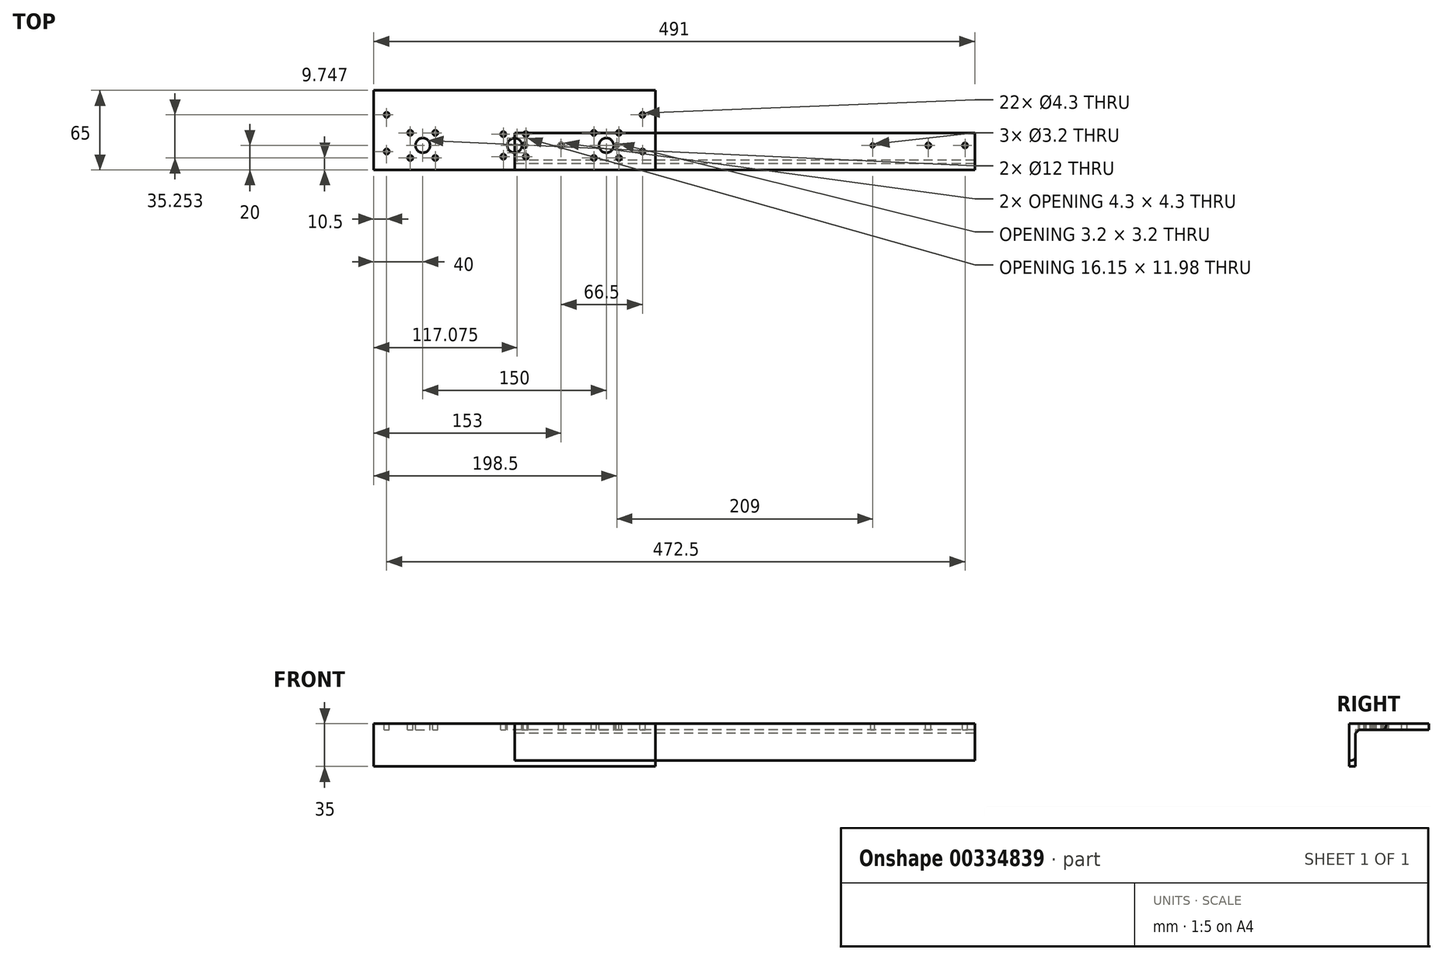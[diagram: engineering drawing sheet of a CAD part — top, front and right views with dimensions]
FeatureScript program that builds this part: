
annotation { "Feature Type Name" : "Feature", "Feature Type Description" : "" }
export const myFeature = defineFeature(function(context is Context, id is Id, definition is map)
    precondition{}
    {
        {
            var Q0;
            Q0=qCreatedBy(makeId("Right.planeOp"),FACE);
            var sketch = newSketch(context, id + "F0", { "sketchPlane" : qUnion([Q0])});
            skLineSegment(sketch, "E0", {"start": v(0, -35) * mm, "end": v(0, 0) * mm});
            skLineSegment(sketch, "E1", {"start": v(0, 0) * mm, "end": v(65, 0) * mm});
            skLineSegment(sketch, "E2", {"start": v(65, 0) * mm, "end": v(65, -5) * mm});
            skLineSegment(sketch, "E3", {"start": v(65, -5) * mm, "end": v(5, -5) * mm});
            skLineSegment(sketch, "E4", {"start": v(5, -5) * mm, "end": v(5, -35) * mm});
            skLineSegment(sketch, "E5", {"start": v(5, -35) * mm, "end": v(0, -35) * mm});
            skSolve(sketch);
        }
        {
            var Q0;
            Q0=qCreatedBy(makeId("Right.planeOp"),FACE);
            var sketch = newSketch(context, id + "F1", { "sketchPlane" : qUnion([Q0])});
            skLineSegment(sketch, "E6", {"start": v(0, -30) * mm, "end": v(0, 0) * mm});
            skLineSegment(sketch, "E7", {"start": v(0, 0) * mm, "end": v(30, 0) * mm});
            skLineSegment(sketch, "E8", {"start": v(30, 0) * mm, "end": v(30, -2) * mm});
            skLineSegment(sketch, "E9", {"start": v(27, -5) * mm, "end": v(5, -5) * mm});
            skLineSegment(sketch, "E10", {"start": v(5, -5) * mm, "end": v(5, -27) * mm});
            skLineSegment(sketch, "E11", {"start": v(2, -30) * mm, "end": v(0, -30) * mm});
            skPoint(sketch, "E12.visualSharp", {"position": v(30, -5) * mm});
            skArc(sketch, "E12.filletArc", {"start": v(27, -5) * mm, "mid": v(29.12, -4.12) * mm, "end": v(30, -2) * mm});
            skPoint(sketch, "E13.visualSharp", {"position": v(5, -30) * mm});
            skArc(sketch, "E13.filletArc", {"start": v(2, -30) * mm, "mid": v(4.12, -29.12) * mm, "end": v(5, -27) * mm});
            skLineSegment(sketch, "E14", {"start": v(5, -8) * mm, "end": v(8, -5) * mm});
            skSolve(sketch);
        }
        {
            var Q0;
            Q0=qCreatedBy(makeId("Right.planeOp"),FACE);
            var sketch = newSketch(context, id + "F2", { "sketchPlane" : qUnion([Q0])});
            skLineSegment(sketch, "E15", {"start": v(0, 0) * mm, "end": v(20, 0) * mm});
            skLineSegment(sketch, "E16", {"start": v(20, 0) * mm, "end": v(20, 0) * mm});
            skLineSegment(sketch, "E17", {"start": v(17, -3) * mm, "end": v(6, -3) * mm});
            skLineSegment(sketch, "E18", {"start": v(3, -6) * mm, "end": v(3, -17) * mm});
            skLineSegment(sketch, "E19", {"start": v(0, -20) * mm, "end": v(0, -20) * mm});
            skLineSegment(sketch, "E20", {"start": v(0, -20) * mm, "end": v(0, 0) * mm});
            skPoint(sketch, "E21.visualSharp", {"position": v(3, -3) * mm});
            skArc(sketch, "E21.filletArc", {"start": v(6, -3) * mm, "mid": v(3.88, -3.88) * mm, "end": v(3, -6) * mm});
            skPoint(sketch, "E22.visualSharp", {"position": v(3, -20) * mm});
            skArc(sketch, "E22.filletArc", {"start": v(0, -20) * mm, "mid": v(2.12, -19.12) * mm, "end": v(3, -17) * mm});
            skPoint(sketch, "E23.visualSharp", {"position": v(20, -3) * mm});
            skArc(sketch, "E23.filletArc", {"start": v(17, -3) * mm, "mid": v(19.12, -2.12) * mm, "end": v(20, 0) * mm});
            skSolve(sketch);
        }
        {
            assignVariable(context, id + "F3", {"name" : "Z_DISTANCE", "anyValue" : 350});
        }
        {
            var Q0;
            Q0 = qSketchRegion(id + "F0", true);
            extrude(context, id + "F4", {"entities" : qUnion([Q0]), "endBound" : BoundingType.SYMMETRIC, "offsetDistance" : 25 * mm, "depth" : 230 * mm});
        }
        {
            var Q0;
            Q0=makeQuery(id+"F4.opExtrude","SWEPT_FACE",FACE,{"disambiguationData":[OSD([sQuery(id+"F0.wireOp",EDGE,"E1")])]});
            var sketch = newSketch(context, id + "F5", { "sketchPlane" : qUnion([Q0])});
            skLineSegment(sketch, "E24", {"start": v(-85.49, 20) * mm, "end": v(94.64, 20) * mm, "construction": true});
            skLineSegment(sketch, "E25", {"start": v(-104.5, 57.4) * mm, "end": v(-104.5, 14.4) * mm, "construction": true});
            skLineSegment(sketch, "E26", {"start": v(0, 45.73) * mm, "end": v(0, 78.01) * mm, "construction": true});
            skPoint(sketch, "E26.endSnap0", {"position": v(0, 65) * mm});
            skSolve(sketch);
        }
        {
            var Q0;
            Q0=makeQuery(id+"F4.opExtrude","SWEPT_FACE",FACE,{"disambiguationData":[OSD([sQuery(id+"F0.wireOp",EDGE,"E1")])]});
            var sketch = newSketch(context, id + "F6", { "sketchPlane" : qUnion([Q0])});
            skCircle(sketch, "E27", {"center": v(0, 20) * mm, "radius": 6 * mm});
            skCircle(sketch, "E28", {"center": v(0, 20) * mm, "radius": 13 * mm, "construction": true});
            skCircle(sketch, "E29", {"center": v(9.2, 29.2) * mm, "radius": 2.15 * mm});
            skCircle(sketch, "E30.1.0", {"center": v(-9.2, 29.2) * mm, "radius": 2.15 * mm});
            skCircle(sketch, "E30.2.0", {"center": v(-9.2, 10.8) * mm, "radius": 2.15 * mm});
            skCircle(sketch, "E30.3.0", {"center": v(9.2, 10.8) * mm, "radius": 2.15 * mm});
            skCircle(sketch, "E31", {"center": v(0, 20) * mm, "radius": 18 * mm, "construction": true});
            skSolve(sketch);
        }
        {
            var Q0;
            Q0=makeQuery(id+"F4.opExtrude","SWEPT_FACE",FACE,{"disambiguationData":[OSD([sQuery(id+"F0.wireOp",EDGE,"E1")])]});
            var sketch = newSketch(context, id + "F7", { "sketchPlane" : qUnion([Q0])});
            skCircle(sketch, "E32", {"center": v(-75, 20) * mm, "radius": 6 * mm});
            skCircle(sketch, "E33", {"center": v(-75, 20) * mm, "radius": 14.5 * mm, "construction": true});
            skCircle(sketch, "E34", {"center": v(-64.75, 30.25) * mm, "radius": 2.15 * mm});
            skCircle(sketch, "E35.1.0", {"center": v(-85.25, 30.25) * mm, "radius": 2.15 * mm});
            skCircle(sketch, "E35.2.0", {"center": v(-85.25, 9.75) * mm, "radius": 2.15 * mm});
            skCircle(sketch, "E35.3.0", {"center": v(-64.75, 9.75) * mm, "radius": 2.15 * mm});
            skLineSegment(sketch, "E36", {"start": v(0, 95.18) * mm, "end": v(0, 48.3) * mm, "construction": true});
            skCircle(sketch, "E37", {"center": v(-75, 20) * mm, "radius": 19.5 * mm, "construction": true});
            skCircle(sketch, "E38.MirrorC", {"center": v(64.75, 9.75) * mm, "radius": 2.15 * mm});
            skCircle(sketch, "E39.MirrorC", {"center": v(85.25, 9.75) * mm, "radius": 2.15 * mm});
            skCircle(sketch, "E40.MirrorC", {"center": v(85.25, 30.25) * mm, "radius": 2.15 * mm});
            skCircle(sketch, "E41.MirrorC", {"center": v(64.75, 30.25) * mm, "radius": 2.15 * mm});
            skCircle(sketch, "E42.MirrorC", {"center": v(75, 20) * mm, "radius": 14.5 * mm, "construction": true});
            skCircle(sketch, "E43.MirrorC", {"center": v(75, 20) * mm, "radius": 19.5 * mm, "construction": true});
            skCircle(sketch, "E44.MirrorC", {"center": v(75, 20) * mm, "radius": 6 * mm});
            skSolve(sketch);
        }
        {
            var Q0;
            Q0 = qSketchRegion(id + "F6", true);
            extrude(context, id + "F8", {"entities" : qUnion([Q0]), "operationType" : NewBodyOperationType.REMOVE, "oppositeDirection" : true, "depth" : 25 * mm});
        }
        {
            var Q0;
            Q0 = qSketchRegion(id + "F7", true);
            extrude(context, id + "F9", {"entities" : qUnion([Q0]), "operationType" : NewBodyOperationType.REMOVE, "oppositeDirection" : true, "depth" : 25 * mm});
        }
        {
            var Q0;
            Q0 = qSketchRegion(id + "F1", true);
            extrude(context, id + "F10", {"entities" : qUnion([Q0]), "depth" : (getVariable(context, 'Z_DISTANCE') + (13) * 2) * mm});
        }
        {
            var Q0;
            Q0=makeQuery(id+"F4.opExtrude","SWEPT_FACE",FACE,{"disambiguationData":[OSD([sQuery(id+"F0.wireOp",EDGE,"E1")])]});
            var sketch = newSketch(context, id + "F11", { "sketchPlane" : qUnion([Q0])});
            skCircle(sketch, "E45", {"center": v(-104.5, 45) * mm, "radius": 2.15 * mm});
            skCircle(sketch, "E46", {"center": v(-104.5, 15) * mm, "radius": 2.15 * mm});
            skCircle(sketch, "E47.MirrorC", {"center": v(104.5, 45) * mm, "radius": 2.15 * mm});
            skCircle(sketch, "E48.MirrorC", {"center": v(104.5, 15) * mm, "radius": 2.15 * mm});
            skSolve(sketch);
        }
        {
            var Q0;
            Q0 = qSketchRegion(id + "F11", true);
            extrude(context, id + "F12", {"entities" : qUnion([Q0]), "operationType" : NewBodyOperationType.REMOVE, "oppositeDirection" : true, "depth" : 25 * mm});
        }
        {
            var Q0;
            Q0=makeQuery(id+"F10.opExtrude","SWEPT_FACE",FACE,{"disambiguationData":[OSD([sQuery(id+"F1.wireOp",EDGE,"E7")])]});
            var sketch = newSketch(context, id + "F13", { "sketchPlane" : qUnion([Q0])});
            skLineSegment(sketch, "E49", {"start": v(188, 27.1) * mm, "end": v(188, 80.73) * mm, "construction": true});
            skLineSegment(sketch, "E50", {"start": v(6.59, 20) * mm, "end": v(14.04, 20) * mm, "construction": true});
            skCircle(sketch, "E51", {"center": v(8, 20) * mm, "radius": 2.15 * mm});
            skCircle(sketch, "E52", {"center": v(38, 20) * mm, "radius": 2.15 * mm});
            skCircle(sketch, "E53.MirrorC", {"center": v(368, 20) * mm, "radius": 2.15 * mm});
            skCircle(sketch, "E54.MirrorC", {"center": v(338, 20) * mm, "radius": 2.15 * mm});
            skLineSegment(sketch, "E55", {"start": v(8, 20) * mm, "end": v(38, 20) * mm, "construction": true});
            skPoint(sketch, "E56", {"position": v(23, 20) * mm});
            skSolve(sketch);
        }
        {
            var Q0;
            Q0 = qSketchRegion(id + "F13", true);
            extrude(context, id + "F14", {"entities" : qUnion([Q0]), "operationType" : NewBodyOperationType.REMOVE, "oppositeDirection" : true, "depth" : 25 * mm});
        }
        {
            var Q0;
            Q0=makeQuery(id+"F10.opExtrude","SWEPT_FACE",FACE,{"disambiguationData":[OSD([sQuery(id+"F1.wireOp",EDGE,"E7")])]});
            var sketch = newSketch(context, id + "F15", { "sketchPlane" : qUnion([Q0])});
            skLineSegment(sketch, "E57", {"start": v(188, 20) * mm, "end": v(188, 86.64) * mm, "construction": true});
            skCircle(sketch, "E58", {"center": v(83.5, 20) * mm, "radius": 1.6 * mm});
            skLineSegment(sketch, "E59", {"start": v(-32, 20) * mm, "end": v(23.54, 20) * mm, "construction": true});
            skCircle(sketch, "E60.MirrorC", {"center": v(292.5, 20) * mm, "radius": 1.6 * mm});
            skSolve(sketch);
        }
        {
            var Q0;
            Q0 = qSketchRegion(id + "F15", true);
            extrude(context, id + "F16", {"entities" : qUnion([Q0]), "operationType" : NewBodyOperationType.REMOVE, "oppositeDirection" : true, "depth" : 25 * mm});
        }
    });
